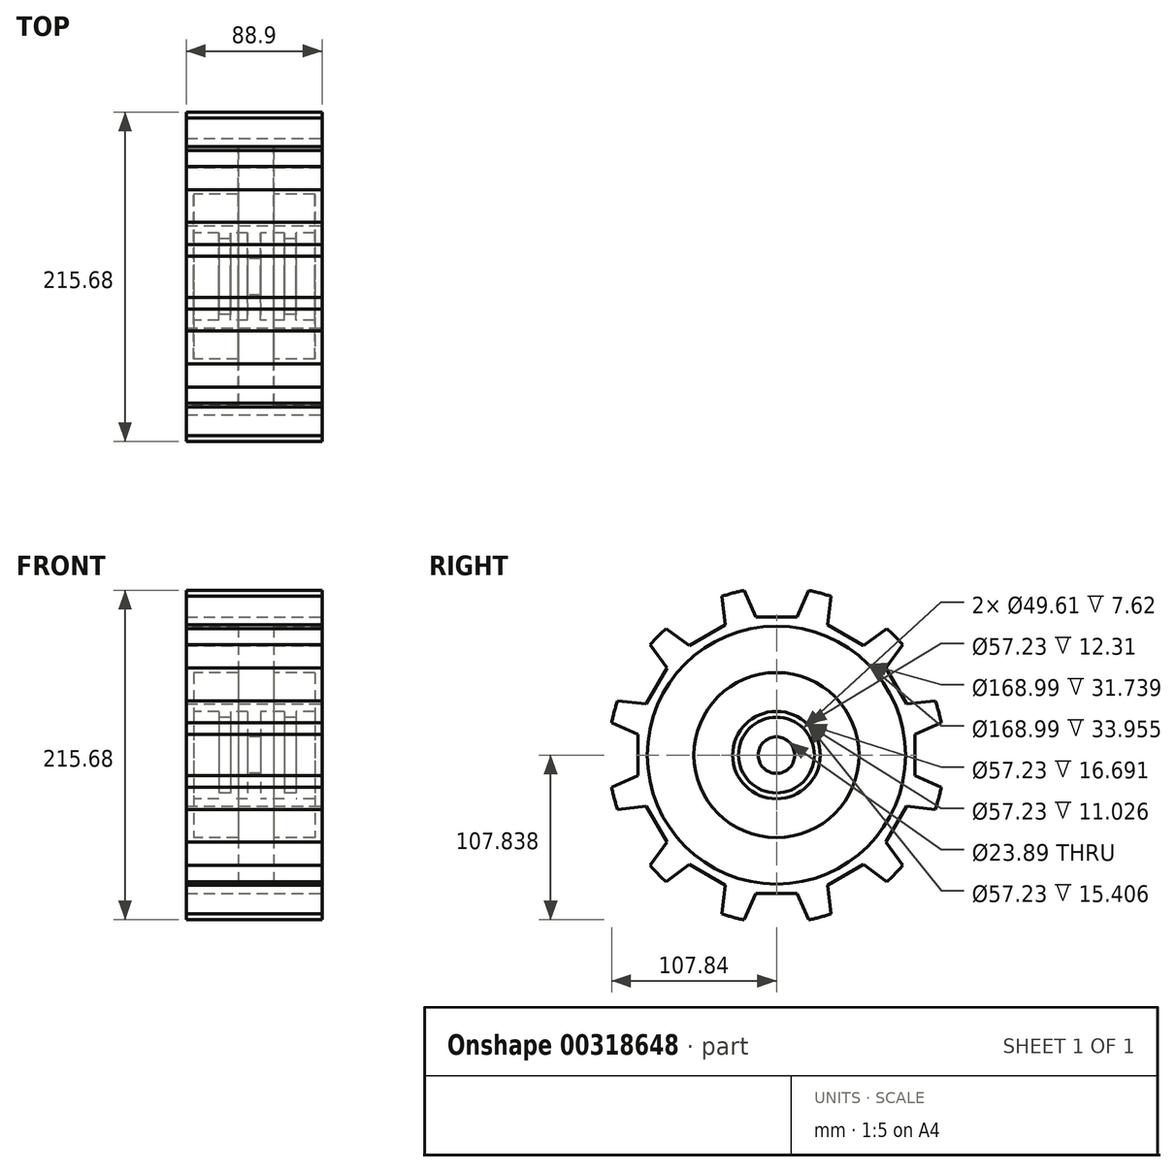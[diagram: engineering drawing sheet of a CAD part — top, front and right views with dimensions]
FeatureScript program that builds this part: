
annotation { "Feature Type Name" : "Feature", "Feature Type Description" : "" }
export const myFeature = defineFeature(function(context is Context, id is Id, definition is map)
    precondition{}
    {
        {
            var Q0;
            Q0=qCreatedBy(makeId("Front.planeOp"),FACE);
            var sketch = newSketch(context, id + "F0", { "sketchPlane" : qUnion([Q0])});
            skLineSegment(sketch, "E0.bottom", {"start": v(44.45, 42.42) * mm, "end": v(-44.45, 42.42) * mm});
            skLineSegment(sketch, "E0.top", {"start": v(44.45, 17.02) * mm, "end": v(12.71, 17.02) * mm});
            skLineSegment(sketch, "E0.left", {"start": v(44.45, 42.42) * mm, "end": v(44.45, 17.02) * mm});
            skLineSegment(sketch, "E0.right", {"start": v(-44.45, 42.42) * mm, "end": v(-44.45, 17.02) * mm});
            skPoint(sketch, "E0.middle", {"position": v(0, 29.72) * mm});
            skPoint(sketch, "E1.middle", {"position": v(0, 13.13) * mm});
            skLineSegment(sketch, "E2.bottom", {"start": v(39.63, -13.46) * mm, "end": v(12.71, -13.46) * mm});
            skLineSegment(sketch, "E2.top", {"start": v(39.63, -38.86) * mm, "end": v(27.32, -38.86) * mm});
            skLineSegment(sketch, "E2.left", {"start": v(39.63, -13.46) * mm, "end": v(39.63, -38.86) * mm});
            skLineSegment(sketch, "E2.right", {"start": v(-39.63, -13.46) * mm, "end": v(-39.63, -38.86) * mm});
            skPoint(sketch, "E2.middle", {"position": v(0, -26.16) * mm});
            skLineSegment(sketch, "E3.bottom", {"start": v(-15.32, -42.67) * mm, "end": v(-22.94, -42.67) * mm});
            skLineSegment(sketch, "E3.left", {"start": v(-15.32, -42.67) * mm, "end": v(-15.32, -38.86) * mm});
            skLineSegment(sketch, "E3.right", {"start": v(-22.94, -42.67) * mm, "end": v(-22.94, -38.86) * mm});
            skPoint(sketch, "E3.middle", {"position": v(-19.13, -38.86) * mm});
            skLineSegment(sketch, "E4.bottom", {"start": v(4.3, -55.53) * mm, "end": v(-4.3, -55.53) * mm});
            skLineSegment(sketch, "E4.left", {"start": v(4.3, -55.53) * mm, "end": v(4.3, -38.86) * mm});
            skLineSegment(sketch, "E4.right", {"start": v(-4.3, -55.53) * mm, "end": v(-4.3, -38.86) * mm});
            skPoint(sketch, "E4.middle", {"position": v(0, -38.86) * mm});
            skLineSegment(sketch, "E5.bottom", {"start": v(27.32, -42.67) * mm, "end": v(19.7, -42.67) * mm});
            skLineSegment(sketch, "E5.left", {"start": v(27.32, -42.67) * mm, "end": v(27.32, -38.86) * mm});
            skLineSegment(sketch, "E5.right", {"start": v(19.7, -42.67) * mm, "end": v(19.7, -38.86) * mm});
            skPoint(sketch, "E5.middle", {"position": v(23.5, -38.86) * mm});
            skPoint(sketch, "E6.orphan", {"position": v(-15.32, -35.05) * mm});
            skPoint(sketch, "E7.orphan", {"position": v(-22.94, -35.05) * mm});
            skPoint(sketch, "E4.top.end.orphan", {"position": v(-4.3, -22.19) * mm});
            skPoint(sketch, "E8.orphan", {"position": v(4.3, -22.19) * mm});
            skPoint(sketch, "E9.orphan", {"position": v(19.7, -35.05) * mm});
            skPoint(sketch, "E10.orphan", {"position": v(27.32, -35.05) * mm});
            skLineSegment(sketch, "E11.trimOffspring", {"start": v(-22.94, -38.86) * mm, "end": v(-39.63, -38.86) * mm});
            skLineSegment(sketch, "E12.trimOffspring", {"start": v(-4.3, -38.86) * mm, "end": v(-15.32, -38.86) * mm});
            skLineSegment(sketch, "E13.trimOffspring", {"start": v(19.7, -38.86) * mm, "end": v(4.3, -38.86) * mm});
            skLineSegment(sketch, "E14", {"start": v(-10.5, 17.02) * mm, "end": v(-10.5, -13.46) * mm});
            skLineSegment(sketch, "E15", {"start": v(12.71, 17.02) * mm, "end": v(12.71, -13.46) * mm});
            skLineSegment(sketch, "E16", {"start": v(-8.85, -67.47) * mm, "end": v(14.3, -67.47) * mm});
            skLineSegment(sketch, "E17.trimOffspring", {"start": v(-10.5, 17.02) * mm, "end": v(-44.45, 17.02) * mm});
            skLineSegment(sketch, "E18.trimOffspring", {"start": v(-10.5, -13.46) * mm, "end": v(-39.63, -13.46) * mm});
            skSolve(sketch);
        }
        {
            var Q0;
            Q0=makeQuery(id+"F0.imprint","IMPRINT",FACE,{"disambiguationData":[TD([[makeQuery(id+"F0.imprint","IMPRINT",EDGE,{"derivedFrom":sQuery(id+"F0.wireOp",EDGE,"E0.bottom")}),1.0]])]});
            var Q1;
            Q1=sQuery(id+"F0.wireOp",EDGE,"E16");
            revolve(context, id + "F1", {"entities" : qUnion([Q0]), "axis" : qUnion([Q1]), "revolveType" : RevolveType.FULL});
        }
        {
            var Q0;
            Q0=qCreatedBy(makeId("Right.planeOp"),FACE);
            var sketch = newSketch(context, id + "F2", { "sketchPlane" : qUnion([Q0])});
            skLineSegment(sketch, "E19", {"start": v(0, -60.75) * mm, "end": v(0, 55.11) * mm, "construction": true});
            skLineSegment(sketch, "E20", {"start": v(13.56, 23.07) * mm, "end": v(24.65, 48.33) * mm});
            skLineSegment(sketch, "E21.MirrorCS", {"start": v(-13.56, 23.07) * mm, "end": v(-24.65, 48.33) * mm});
            skLineSegment(sketch, "E22", {"start": v(-24.65, 48.33) * mm, "end": v(24.65, 48.33) * mm});
            skLineSegment(sketch, "E23", {"start": v(-13.56, 23.07) * mm, "end": v(13.56, 23.07) * mm});
            skSolve(sketch);
        }
        {
            var Q0;
            Q0=makeQuery(id+"F2.imprint","IMPRINT",FACE,{"disambiguationData":[TD([[makeQuery(id+"F2.imprint","IMPRINT",EDGE,{"derivedFrom":sQuery(id+"F2.wireOp",EDGE,"E20")}),1.0]])]});
            extrude(context, id + "F3", {"entities" : qUnion([Q0]), "operationType" : NewBodyOperationType.REMOVE, "endBound" : BoundingType.SYMMETRIC, "oppositeDirection" : true, "depth" : 91.44 * mm});
        }
        {
            var Q0;
            Q0=makeQuery(id+"F3.boolean.opBoolean","COPY",FACE,{"derivedFrom":makeQuery(id+"F3.opExtrude","SWEPT_FACE",FACE,{"disambiguationData":[OSD([sQuery(id+"F2.wireOp",EDGE,"E20")])]})});
            var Q1;
            Q1=makeQuery(id+"F3.boolean.opBoolean","COPY",FACE,{"derivedFrom":makeQuery(id+"F3.opExtrude","SWEPT_FACE",FACE,{"disambiguationData":[OSD([sQuery(id+"F2.wireOp",EDGE,"E23")])]})});
            var Q2;
            Q2=makeQuery(id+"F3.boolean.opBoolean","COPY",FACE,{"derivedFrom":makeQuery(id+"F3.opExtrude","SWEPT_FACE",FACE,{"disambiguationData":[OSD([sQuery(id+"F2.wireOp",EDGE,"E21.MirrorCS")])]})});
            var Q3;
            Q3=makeQuery(id+"F1.opRevolve","SWEPT_EDGE",EDGE,{"disambiguationData":[OSD([sQuery(id+"F0.wireOp",EDGE,"E0.top"),sQuery(id+"F0.wireOp",EDGE,"E0.left")])]});
            circularPattern(context, id + "F4", {"patternType" : PatternType.FACE, "faces" : qUnion([Q0, Q1, Q2]), "axis" : qUnion([Q3]), "angle" : 360 * degree, "instanceCount" : 12, "equalSpace" : true});
        }
    });
